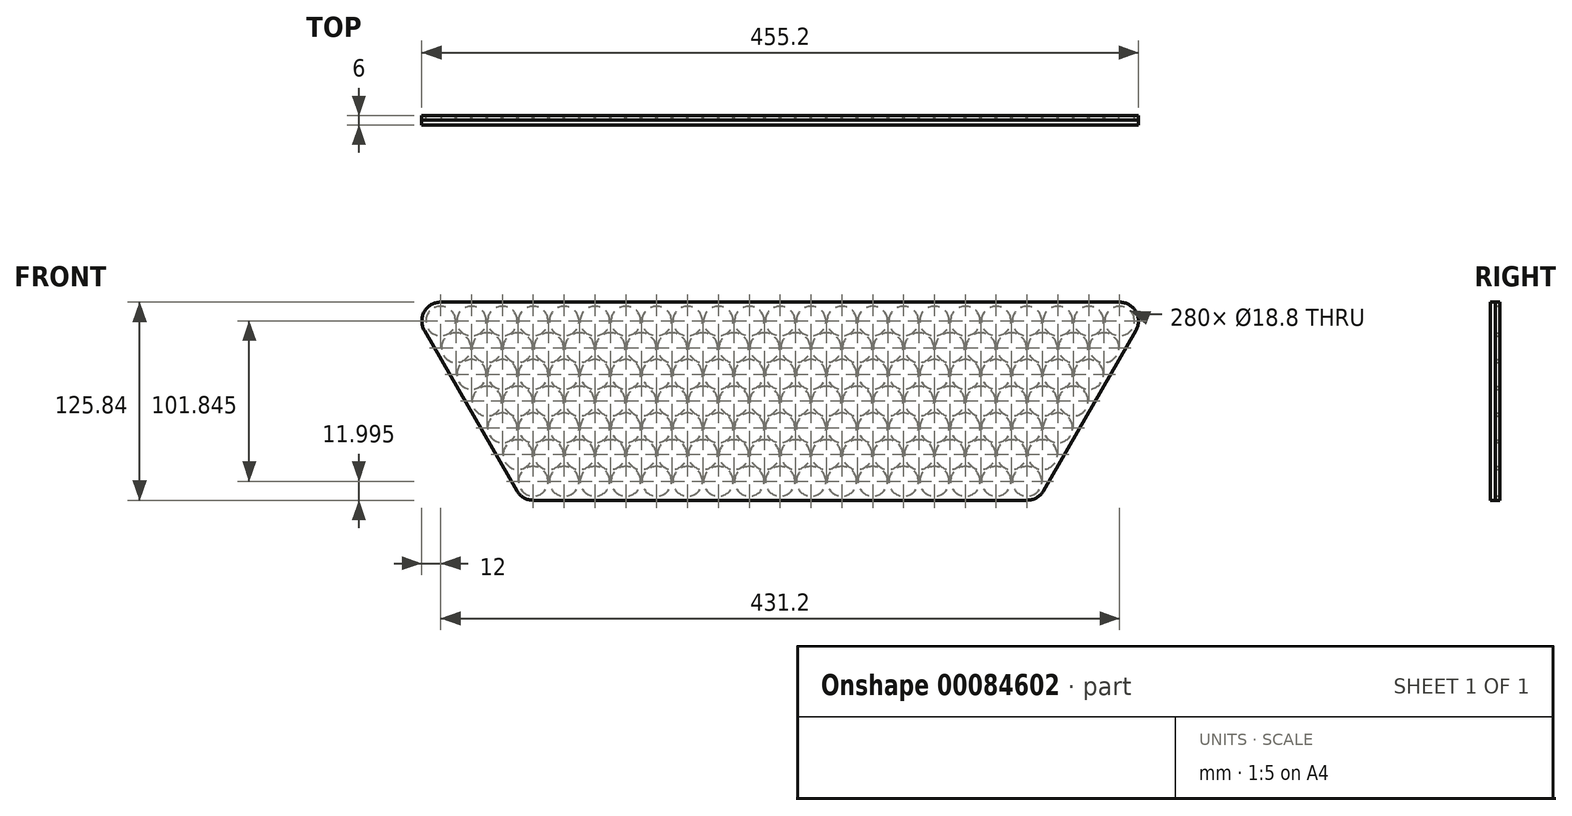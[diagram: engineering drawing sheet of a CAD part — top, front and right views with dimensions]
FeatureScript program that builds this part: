
annotation { "Feature Type Name" : "Feature", "Feature Type Description" : "" }
export const myFeature = defineFeature(function(context is Context, id is Id, definition is map)
    precondition{}
    {
        {
            var Q0;
            Q0=qCreatedBy(makeId("Front.planeOp"),FACE);
            var sketch = newSketch(context, id + "F0", { "sketchPlane" : qUnion([Q0]) });
            skLineSegment(sketch, "E0", {"start": v(0, 0) * mm, "end": v(79.44, 0) * mm, "construction": true});
            skLineSegment(sketch, "E1", {"start": v(0, 0) * mm, "end": v(43.4, -75.16) * mm, "construction": true});
            skCircle(sketch, "E2", {"center": v(0, 0) * mm, "radius": 9.4 * mm});
            skCircle(sketch, "E3.1.0.0", {"center": v(19.6, 0) * mm, "radius": 9.4 * mm});
            skCircle(sketch, "E3.2.0.0", {"center": v(39.2, 0) * mm, "radius": 9.4 * mm});
            skCircle(sketch, "E3.3.0.0", {"center": v(58.8, 0) * mm, "radius": 9.4 * mm});
            skCircle(sketch, "E3.4.0.0", {"center": v(78.4, 0) * mm, "radius": 9.4 * mm});
            skCircle(sketch, "E3.5.0.0", {"center": v(98, 0) * mm, "radius": 9.4 * mm});
            skCircle(sketch, "E3.6.0.0", {"center": v(117.6, 0) * mm, "radius": 9.4 * mm});
            skCircle(sketch, "E3.7.0.0", {"center": v(137.2, 0) * mm, "radius": 9.4 * mm});
            skCircle(sketch, "E3.8.0.0", {"center": v(156.8, 0) * mm, "radius": 9.4 * mm});
            skCircle(sketch, "E3.9.0.0", {"center": v(176.4, 0) * mm, "radius": 9.4 * mm});
            skCircle(sketch, "E3.10.0.0", {"center": v(196, 0) * mm, "radius": 9.4 * mm});
            skCircle(sketch, "E3.11.0.0", {"center": v(215.6, 0) * mm, "radius": 9.4 * mm});
            skCircle(sketch, "E3.12.0.0", {"center": v(235.2, 0) * mm, "radius": 9.4 * mm});
            skCircle(sketch, "E3.13.0.0", {"center": v(254.8, 0) * mm, "radius": 9.4 * mm});
            skCircle(sketch, "E3.14.0.0", {"center": v(274.4, 0) * mm, "radius": 9.4 * mm});
            skCircle(sketch, "E3.15.0.0", {"center": v(294, 0) * mm, "radius": 9.4 * mm});
            skCircle(sketch, "E3.16.0.0", {"center": v(313.6, 0) * mm, "radius": 9.4 * mm});
            skCircle(sketch, "E3.17.0.0", {"center": v(333.2, 0) * mm, "radius": 9.4 * mm});
            skCircle(sketch, "E3.18.0.0", {"center": v(352.8, 0) * mm, "radius": 9.4 * mm});
            skCircle(sketch, "E3.19.0.0", {"center": v(372.4, 0) * mm, "radius": 9.4 * mm});
            skLineSegment(sketch, "E3.direction1", {"start": v(0, 0) * mm, "end": v(19.6, 0) * mm, "construction": true});
            skCircle(sketch, "E4.1.0.0", {"center": v(9.8, -16.97) * mm, "radius": 9.4 * mm});
            skCircle(sketch, "E4.2.0.0", {"center": v(19.6, -33.95) * mm, "radius": 9.4 * mm});
            skCircle(sketch, "E4.3.0.0", {"center": v(29.4, -50.92) * mm, "radius": 9.4 * mm});
            skCircle(sketch, "E4.4.0.0", {"center": v(39.2, -67.9) * mm, "radius": 9.4 * mm});
            skCircle(sketch, "E4.5.0.0", {"center": v(49, -84.87) * mm, "radius": 9.4 * mm});
            skCircle(sketch, "E4.6.0.0", {"center": v(58.8, -101.84) * mm, "radius": 9.4 * mm});
            skLineSegment(sketch, "E4.direction1", {"start": v(0, 0) * mm, "end": v(9.8, -16.97) * mm, "construction": true});
            skCircle(sketch, "E5.1.0.0", {"center": v(29.4, -16.97) * mm, "radius": 9.4 * mm});
            skCircle(sketch, "E5.1.0.1", {"center": v(39.2, -33.95) * mm, "radius": 9.4 * mm});
            skCircle(sketch, "E5.1.0.2", {"center": v(49, -50.92) * mm, "radius": 9.4 * mm});
            skCircle(sketch, "E5.1.0.3", {"center": v(58.8, -67.9) * mm, "radius": 9.4 * mm});
            skCircle(sketch, "E5.1.0.4", {"center": v(68.6, -84.87) * mm, "radius": 9.4 * mm});
            skCircle(sketch, "E5.1.0.5", {"center": v(78.4, -101.84) * mm, "radius": 9.4 * mm});
            skCircle(sketch, "E5.2.0.0", {"center": v(49, -16.97) * mm, "radius": 9.4 * mm});
            skCircle(sketch, "E5.2.0.1", {"center": v(58.8, -33.95) * mm, "radius": 9.4 * mm});
            skCircle(sketch, "E5.2.0.2", {"center": v(68.6, -50.92) * mm, "radius": 9.4 * mm});
            skCircle(sketch, "E5.2.0.3", {"center": v(78.4, -67.9) * mm, "radius": 9.4 * mm});
            skCircle(sketch, "E5.2.0.4", {"center": v(88.2, -84.87) * mm, "radius": 9.4 * mm});
            skCircle(sketch, "E5.2.0.5", {"center": v(98, -101.84) * mm, "radius": 9.4 * mm});
            skCircle(sketch, "E5.3.0.0", {"center": v(68.6, -16.97) * mm, "radius": 9.4 * mm});
            skCircle(sketch, "E5.3.0.1", {"center": v(78.4, -33.95) * mm, "radius": 9.4 * mm});
            skCircle(sketch, "E5.3.0.2", {"center": v(88.2, -50.92) * mm, "radius": 9.4 * mm});
            skCircle(sketch, "E5.3.0.3", {"center": v(98, -67.9) * mm, "radius": 9.4 * mm});
            skCircle(sketch, "E5.3.0.4", {"center": v(107.8, -84.87) * mm, "radius": 9.4 * mm});
            skCircle(sketch, "E5.3.0.5", {"center": v(117.6, -101.84) * mm, "radius": 9.4 * mm});
            skCircle(sketch, "E5.4.0.0", {"center": v(88.2, -16.97) * mm, "radius": 9.4 * mm});
            skCircle(sketch, "E5.4.0.1", {"center": v(98, -33.95) * mm, "radius": 9.4 * mm});
            skCircle(sketch, "E5.4.0.2", {"center": v(107.8, -50.92) * mm, "radius": 9.4 * mm});
            skCircle(sketch, "E5.4.0.3", {"center": v(117.6, -67.9) * mm, "radius": 9.4 * mm});
            skCircle(sketch, "E5.4.0.4", {"center": v(127.4, -84.87) * mm, "radius": 9.4 * mm});
            skCircle(sketch, "E5.4.0.5", {"center": v(137.2, -101.84) * mm, "radius": 9.4 * mm});
            skCircle(sketch, "E5.5.0.0", {"center": v(107.8, -16.97) * mm, "radius": 9.4 * mm});
            skCircle(sketch, "E5.5.0.1", {"center": v(117.6, -33.95) * mm, "radius": 9.4 * mm});
            skCircle(sketch, "E5.5.0.2", {"center": v(127.4, -50.92) * mm, "radius": 9.4 * mm});
            skCircle(sketch, "E5.5.0.3", {"center": v(137.2, -67.9) * mm, "radius": 9.4 * mm});
            skCircle(sketch, "E5.5.0.4", {"center": v(147, -84.87) * mm, "radius": 9.4 * mm});
            skCircle(sketch, "E5.5.0.5", {"center": v(156.8, -101.84) * mm, "radius": 9.4 * mm});
            skCircle(sketch, "E5.6.0.0", {"center": v(127.4, -16.97) * mm, "radius": 9.4 * mm});
            skCircle(sketch, "E5.6.0.1", {"center": v(137.2, -33.95) * mm, "radius": 9.4 * mm});
            skCircle(sketch, "E5.6.0.2", {"center": v(147, -50.92) * mm, "radius": 9.4 * mm});
            skCircle(sketch, "E5.6.0.3", {"center": v(156.8, -67.9) * mm, "radius": 9.4 * mm});
            skCircle(sketch, "E5.6.0.4", {"center": v(166.6, -84.87) * mm, "radius": 9.4 * mm});
            skCircle(sketch, "E5.6.0.5", {"center": v(176.4, -101.84) * mm, "radius": 9.4 * mm});
            skCircle(sketch, "E5.7.0.0", {"center": v(147, -16.97) * mm, "radius": 9.4 * mm});
            skCircle(sketch, "E5.7.0.1", {"center": v(156.8, -33.95) * mm, "radius": 9.4 * mm});
            skCircle(sketch, "E5.7.0.2", {"center": v(166.6, -50.92) * mm, "radius": 9.4 * mm});
            skCircle(sketch, "E5.7.0.3", {"center": v(176.4, -67.9) * mm, "radius": 9.4 * mm});
            skCircle(sketch, "E5.7.0.4", {"center": v(186.2, -84.87) * mm, "radius": 9.4 * mm});
            skCircle(sketch, "E5.7.0.5", {"center": v(196, -101.84) * mm, "radius": 9.4 * mm});
            skCircle(sketch, "E5.8.0.0", {"center": v(166.6, -16.97) * mm, "radius": 9.4 * mm});
            skCircle(sketch, "E5.8.0.1", {"center": v(176.4, -33.95) * mm, "radius": 9.4 * mm});
            skCircle(sketch, "E5.8.0.2", {"center": v(186.2, -50.92) * mm, "radius": 9.4 * mm});
            skCircle(sketch, "E5.8.0.3", {"center": v(196, -67.9) * mm, "radius": 9.4 * mm});
            skCircle(sketch, "E5.8.0.4", {"center": v(205.8, -84.87) * mm, "radius": 9.4 * mm});
            skCircle(sketch, "E5.8.0.5", {"center": v(215.6, -101.84) * mm, "radius": 9.4 * mm});
            skCircle(sketch, "E5.9.0.0", {"center": v(186.2, -16.97) * mm, "radius": 9.4 * mm});
            skCircle(sketch, "E5.9.0.1", {"center": v(196, -33.95) * mm, "radius": 9.4 * mm});
            skCircle(sketch, "E5.9.0.2", {"center": v(205.8, -50.92) * mm, "radius": 9.4 * mm});
            skCircle(sketch, "E5.9.0.3", {"center": v(215.6, -67.9) * mm, "radius": 9.4 * mm});
            skCircle(sketch, "E5.9.0.4", {"center": v(225.4, -84.87) * mm, "radius": 9.4 * mm});
            skCircle(sketch, "E5.9.0.5", {"center": v(235.2, -101.84) * mm, "radius": 9.4 * mm});
            skCircle(sketch, "E5.10.0.0", {"center": v(205.8, -16.97) * mm, "radius": 9.4 * mm});
            skCircle(sketch, "E5.10.0.1", {"center": v(215.6, -33.95) * mm, "radius": 9.4 * mm});
            skCircle(sketch, "E5.10.0.2", {"center": v(225.4, -50.92) * mm, "radius": 9.4 * mm});
            skCircle(sketch, "E5.10.0.3", {"center": v(235.2, -67.9) * mm, "radius": 9.4 * mm});
            skCircle(sketch, "E5.10.0.4", {"center": v(245, -84.87) * mm, "radius": 9.4 * mm});
            skCircle(sketch, "E5.10.0.5", {"center": v(254.8, -101.84) * mm, "radius": 9.4 * mm});
            skCircle(sketch, "E5.11.0.0", {"center": v(225.4, -16.97) * mm, "radius": 9.4 * mm});
            skCircle(sketch, "E5.11.0.1", {"center": v(235.2, -33.95) * mm, "radius": 9.4 * mm});
            skCircle(sketch, "E5.11.0.2", {"center": v(245, -50.92) * mm, "radius": 9.4 * mm});
            skCircle(sketch, "E5.11.0.3", {"center": v(254.8, -67.9) * mm, "radius": 9.4 * mm});
            skCircle(sketch, "E5.11.0.4", {"center": v(264.6, -84.87) * mm, "radius": 9.4 * mm});
            skCircle(sketch, "E5.11.0.5", {"center": v(274.4, -101.84) * mm, "radius": 9.4 * mm});
            skCircle(sketch, "E5.12.0.0", {"center": v(245, -16.97) * mm, "radius": 9.4 * mm});
            skCircle(sketch, "E5.12.0.1", {"center": v(254.8, -33.95) * mm, "radius": 9.4 * mm});
            skCircle(sketch, "E5.12.0.2", {"center": v(264.6, -50.92) * mm, "radius": 9.4 * mm});
            skCircle(sketch, "E5.12.0.3", {"center": v(274.4, -67.9) * mm, "radius": 9.4 * mm});
            skCircle(sketch, "E5.12.0.4", {"center": v(284.2, -84.87) * mm, "radius": 9.4 * mm});
            skCircle(sketch, "E5.12.0.5", {"center": v(294, -101.84) * mm, "radius": 9.4 * mm});
            skCircle(sketch, "E5.13.0.0", {"center": v(264.6, -16.97) * mm, "radius": 9.4 * mm});
            skCircle(sketch, "E5.13.0.1", {"center": v(274.4, -33.95) * mm, "radius": 9.4 * mm});
            skCircle(sketch, "E5.13.0.2", {"center": v(284.2, -50.92) * mm, "radius": 9.4 * mm});
            skCircle(sketch, "E5.13.0.3", {"center": v(294, -67.9) * mm, "radius": 9.4 * mm});
            skCircle(sketch, "E5.13.0.4", {"center": v(303.8, -84.87) * mm, "radius": 9.4 * mm});
            skCircle(sketch, "E5.13.0.5", {"center": v(313.6, -101.84) * mm, "radius": 9.4 * mm});
            skCircle(sketch, "E5.14.0.0", {"center": v(284.2, -16.97) * mm, "radius": 9.4 * mm});
            skCircle(sketch, "E5.14.0.1", {"center": v(294, -33.95) * mm, "radius": 9.4 * mm});
            skCircle(sketch, "E5.14.0.2", {"center": v(303.8, -50.92) * mm, "radius": 9.4 * mm});
            skCircle(sketch, "E5.14.0.3", {"center": v(313.6, -67.9) * mm, "radius": 9.4 * mm});
            skCircle(sketch, "E5.14.0.4", {"center": v(323.4, -84.87) * mm, "radius": 9.4 * mm});
            skCircle(sketch, "E5.14.0.5", {"center": v(333.2, -101.84) * mm, "radius": 9.4 * mm});
            skCircle(sketch, "E5.15.0.0", {"center": v(303.8, -16.97) * mm, "radius": 9.4 * mm});
            skCircle(sketch, "E5.15.0.1", {"center": v(313.6, -33.95) * mm, "radius": 9.4 * mm});
            skCircle(sketch, "E5.15.0.2", {"center": v(323.4, -50.92) * mm, "radius": 9.4 * mm});
            skCircle(sketch, "E5.15.0.3", {"center": v(333.2, -67.9) * mm, "radius": 9.4 * mm});
            skCircle(sketch, "E5.15.0.4", {"center": v(343, -84.87) * mm, "radius": 9.4 * mm});
            skCircle(sketch, "E5.15.0.5", {"center": v(352.8, -101.84) * mm, "radius": 9.4 * mm});
            skCircle(sketch, "E5.16.0.0", {"center": v(323.4, -16.97) * mm, "radius": 9.4 * mm});
            skCircle(sketch, "E5.16.0.1", {"center": v(333.2, -33.95) * mm, "radius": 9.4 * mm});
            skCircle(sketch, "E5.16.0.2", {"center": v(343, -50.92) * mm, "radius": 9.4 * mm});
            skCircle(sketch, "E5.16.0.3", {"center": v(352.8, -67.9) * mm, "radius": 9.4 * mm});
            skCircle(sketch, "E5.16.0.4", {"center": v(362.6, -84.87) * mm, "radius": 9.4 * mm});
            skCircle(sketch, "E5.16.0.5", {"center": v(372.4, -101.84) * mm, "radius": 9.4 * mm});
            skCircle(sketch, "E5.17.0.0", {"center": v(343, -16.97) * mm, "radius": 9.4 * mm});
            skCircle(sketch, "E5.17.0.1", {"center": v(352.8, -33.95) * mm, "radius": 9.4 * mm});
            skCircle(sketch, "E5.17.0.2", {"center": v(362.6, -50.92) * mm, "radius": 9.4 * mm});
            skCircle(sketch, "E5.17.0.3", {"center": v(372.4, -67.9) * mm, "radius": 9.4 * mm});
            skCircle(sketch, "E5.17.0.4", {"center": v(382.2, -84.87) * mm, "radius": 9.4 * mm});
            skCircle(sketch, "E5.18.0.0", {"center": v(362.6, -16.97) * mm, "radius": 9.4 * mm});
            skCircle(sketch, "E5.18.0.1", {"center": v(372.4, -33.95) * mm, "radius": 9.4 * mm});
            skCircle(sketch, "E5.18.0.2", {"center": v(382.2, -50.92) * mm, "radius": 9.4 * mm});
            skCircle(sketch, "E5.18.0.3", {"center": v(392, -67.9) * mm, "radius": 9.4 * mm});
            skCircle(sketch, "E5.19.0.0", {"center": v(382.2, -16.97) * mm, "radius": 9.4 * mm});
            skCircle(sketch, "E5.19.0.1", {"center": v(392, -33.95) * mm, "radius": 9.4 * mm});
            skCircle(sketch, "E5.19.0.2", {"center": v(401.8, -50.92) * mm, "radius": 9.4 * mm});
            skLineSegment(sketch, "E5.direction1", {"start": v(9.8, -16.97) * mm, "end": v(29.4, -16.97) * mm, "construction": true});
            skLineSegment(sketch, "E6", {"start": v(0, 0) * mm, "end": v(372.4, 0) * mm, "construction": true});
            skLineSegment(sketch, "E7", {"start": v(372.4, 0) * mm, "end": v(441, -118.82) * mm, "construction": true});
            skLineSegment(sketch, "E8", {"start": v(58.8, -101.84) * mm, "end": v(0, 0) * mm, "construction": true});
            skLineSegment(sketch, "E9", {"start": v(58.8, -101.84) * mm, "end": v(431.2, -101.84) * mm, "construction": true});
            skCircle(sketch, "E10.1.0.0", {"center": v(392, 0) * mm, "radius": 9.4 * mm});
            skCircle(sketch, "E10.2.0.0", {"center": v(411.6, 0) * mm, "radius": 9.4 * mm});
            skCircle(sketch, "E10.3.0.0", {"center": v(431.2, 0) * mm, "radius": 9.4 * mm});
            skLineSegment(sketch, "E10.direction1", {"start": v(372.4, 0) * mm, "end": v(392, 0) * mm, "construction": true});
            skCircle(sketch, "E11.1.0.0", {"center": v(401.8, -16.97) * mm, "radius": 9.4 * mm});
            skCircle(sketch, "E11.2.0.0", {"center": v(421.4, -16.97) * mm, "radius": 9.4 * mm});
            skLineSegment(sketch, "E11.direction1", {"start": v(382.2, -16.97) * mm, "end": v(401.8, -16.97) * mm, "construction": true});
            skCircle(sketch, "E12.1.0.0", {"center": v(411.6, -33.95) * mm, "radius": 9.4 * mm});
            skLineSegment(sketch, "E12.direction1", {"start": v(392, -33.95) * mm, "end": v(411.6, -33.95) * mm, "construction": true});
            skArc(sketch, "E13", {"start": v(441.6, -6) * mm, "mid": v(441.6, 6) * mm, "end": v(431.2, 12) * mm});
            skArc(sketch, "E14", {"start": v(372.4, -113.84) * mm, "mid": v(378.4, -112.24) * mm, "end": v(382.8, -107.84) * mm});
            skArc(sketch, "E15", {"start": v(0, 12) * mm, "mid": v(-10.4, 6) * mm, "end": v(-10.4, -6) * mm});
            skArc(sketch, "E16", {"start": v(48.4, -107.84) * mm, "mid": v(52.8, -112.24) * mm, "end": v(58.8, -113.84) * mm});
            skLineSegment(sketch, "E17", {"start": v(441.6, -6) * mm, "end": v(382.8, -107.84) * mm});
            skLineSegment(sketch, "E18", {"start": v(0, 12) * mm, "end": v(431.2, 12) * mm});
            skLineSegment(sketch, "E19", {"start": v(-10.4, -6) * mm, "end": v(48.4, -107.84) * mm});
            skLineSegment(sketch, "E20", {"start": v(58.8, -113.84) * mm, "end": v(372.4, -113.84) * mm});
            skSolve(sketch);
        }
        {
            var Q0;
            Q0=makeQuery(id+"F0.imprint","IMPRINT",FACE,{"disambiguationData":[TD([[makeQuery(id+"F0.imprint","IMPRINT",EDGE,{"derivedFrom":sQuery(id+"F0.wireOp",EDGE,"E2")}),-1.0]])]});
            extrude(context, id + "F1", {"entities" : qUnion([Q0]), "depth" : 3 * mm});
        }
        {
            var Q0;
            Q0=makeQuery(id+"F1.opExtrude","CAP_FACE",FACE,{"disambiguationData":[OSD([sQuery(id+"F0.wireOp",EDGE,"E2"),sQuery(id+"F0.wireOp",EDGE,"E3.1.0.0"),sQuery(id+"F0.wireOp",EDGE,"E3.2.0.0"),sQuery(id+"F0.wireOp",EDGE,"E3.3.0.0"),sQuery(id+"F0.wireOp",EDGE,"E3.4.0.0"),sQuery(id+"F0.wireOp",EDGE,"E3.5.0.0"),sQuery(id+"F0.wireOp",EDGE,"E3.6.0.0"),sQuery(id+"F0.wireOp",EDGE,"E3.7.0.0"),sQuery(id+"F0.wireOp",EDGE,"E3.8.0.0"),sQuery(id+"F0.wireOp",EDGE,"E3.9.0.0"),sQuery(id+"F0.wireOp",EDGE,"E3.10.0.0"),sQuery(id+"F0.wireOp",EDGE,"E3.11.0.0"),sQuery(id+"F0.wireOp",EDGE,"E3.12.0.0"),sQuery(id+"F0.wireOp",EDGE,"E3.13.0.0"),sQuery(id+"F0.wireOp",EDGE,"E3.14.0.0"),sQuery(id+"F0.wireOp",EDGE,"E3.15.0.0"),sQuery(id+"F0.wireOp",EDGE,"E3.16.0.0"),sQuery(id+"F0.wireOp",EDGE,"E3.17.0.0"),sQuery(id+"F0.wireOp",EDGE,"E3.18.0.0"),sQuery(id+"F0.wireOp",EDGE,"E3.19.0.0"),sQuery(id+"F0.wireOp",EDGE,"E4.1.0.0"),sQuery(id+"F0.wireOp",EDGE,"E4.2.0.0"),sQuery(id+"F0.wireOp",EDGE,"E4.3.0.0"),sQuery(id+"F0.wireOp",EDGE,"E4.4.0.0"),sQuery(id+"F0.wireOp",EDGE,"E4.5.0.0"),sQuery(id+"F0.wireOp",EDGE,"E4.6.0.0"),sQuery(id+"F0.wireOp",EDGE,"E5.1.0.0"),sQuery(id+"F0.wireOp",EDGE,"E5.1.0.1"),sQuery(id+"F0.wireOp",EDGE,"E5.1.0.2"),sQuery(id+"F0.wireOp",EDGE,"E5.1.0.3"),sQuery(id+"F0.wireOp",EDGE,"E5.1.0.4"),sQuery(id+"F0.wireOp",EDGE,"E5.1.0.5"),sQuery(id+"F0.wireOp",EDGE,"E5.2.0.0"),sQuery(id+"F0.wireOp",EDGE,"E5.2.0.1"),sQuery(id+"F0.wireOp",EDGE,"E5.2.0.2"),sQuery(id+"F0.wireOp",EDGE,"E5.2.0.3"),sQuery(id+"F0.wireOp",EDGE,"E5.2.0.4"),sQuery(id+"F0.wireOp",EDGE,"E5.2.0.5"),sQuery(id+"F0.wireOp",EDGE,"E5.3.0.0"),sQuery(id+"F0.wireOp",EDGE,"E5.3.0.1"),sQuery(id+"F0.wireOp",EDGE,"E5.3.0.2"),sQuery(id+"F0.wireOp",EDGE,"E5.3.0.3"),sQuery(id+"F0.wireOp",EDGE,"E5.3.0.4"),sQuery(id+"F0.wireOp",EDGE,"E5.3.0.5"),sQuery(id+"F0.wireOp",EDGE,"E5.4.0.0"),sQuery(id+"F0.wireOp",EDGE,"E5.4.0.1"),sQuery(id+"F0.wireOp",EDGE,"E5.4.0.2"),sQuery(id+"F0.wireOp",EDGE,"E5.4.0.3"),sQuery(id+"F0.wireOp",EDGE,"E5.4.0.4"),sQuery(id+"F0.wireOp",EDGE,"E5.4.0.5"),sQuery(id+"F0.wireOp",EDGE,"E5.5.0.0"),sQuery(id+"F0.wireOp",EDGE,"E5.5.0.1"),sQuery(id+"F0.wireOp",EDGE,"E5.5.0.2"),sQuery(id+"F0.wireOp",EDGE,"E5.5.0.3"),sQuery(id+"F0.wireOp",EDGE,"E5.5.0.4"),sQuery(id+"F0.wireOp",EDGE,"E5.5.0.5"),sQuery(id+"F0.wireOp",EDGE,"E5.6.0.0"),sQuery(id+"F0.wireOp",EDGE,"E5.6.0.1"),sQuery(id+"F0.wireOp",EDGE,"E5.6.0.2"),sQuery(id+"F0.wireOp",EDGE,"E5.6.0.3"),sQuery(id+"F0.wireOp",EDGE,"E5.6.0.4"),sQuery(id+"F0.wireOp",EDGE,"E5.6.0.5"),sQuery(id+"F0.wireOp",EDGE,"E5.7.0.0"),sQuery(id+"F0.wireOp",EDGE,"E5.7.0.1"),sQuery(id+"F0.wireOp",EDGE,"E5.7.0.2"),sQuery(id+"F0.wireOp",EDGE,"E5.7.0.3"),sQuery(id+"F0.wireOp",EDGE,"E5.7.0.4"),sQuery(id+"F0.wireOp",EDGE,"E5.7.0.5"),sQuery(id+"F0.wireOp",EDGE,"E5.8.0.0"),sQuery(id+"F0.wireOp",EDGE,"E5.8.0.1"),sQuery(id+"F0.wireOp",EDGE,"E5.8.0.2"),sQuery(id+"F0.wireOp",EDGE,"E5.8.0.3"),sQuery(id+"F0.wireOp",EDGE,"E5.8.0.4"),sQuery(id+"F0.wireOp",EDGE,"E5.8.0.5"),sQuery(id+"F0.wireOp",EDGE,"E5.9.0.0"),sQuery(id+"F0.wireOp",EDGE,"E5.9.0.1"),sQuery(id+"F0.wireOp",EDGE,"E5.9.0.2"),sQuery(id+"F0.wireOp",EDGE,"E5.9.0.3"),sQuery(id+"F0.wireOp",EDGE,"E5.9.0.4"),sQuery(id+"F0.wireOp",EDGE,"E5.9.0.5"),sQuery(id+"F0.wireOp",EDGE,"E5.10.0.0"),sQuery(id+"F0.wireOp",EDGE,"E5.10.0.1"),sQuery(id+"F0.wireOp",EDGE,"E5.10.0.2"),sQuery(id+"F0.wireOp",EDGE,"E5.10.0.3"),sQuery(id+"F0.wireOp",EDGE,"E5.10.0.4"),sQuery(id+"F0.wireOp",EDGE,"E5.10.0.5"),sQuery(id+"F0.wireOp",EDGE,"E5.11.0.0"),sQuery(id+"F0.wireOp",EDGE,"E5.11.0.1"),sQuery(id+"F0.wireOp",EDGE,"E5.11.0.2"),sQuery(id+"F0.wireOp",EDGE,"E5.11.0.3"),sQuery(id+"F0.wireOp",EDGE,"E5.11.0.4"),sQuery(id+"F0.wireOp",EDGE,"E5.11.0.5"),sQuery(id+"F0.wireOp",EDGE,"E5.12.0.0"),sQuery(id+"F0.wireOp",EDGE,"E5.12.0.1"),sQuery(id+"F0.wireOp",EDGE,"E5.12.0.2"),sQuery(id+"F0.wireOp",EDGE,"E5.12.0.3"),sQuery(id+"F0.wireOp",EDGE,"E5.12.0.4"),sQuery(id+"F0.wireOp",EDGE,"E5.12.0.5"),sQuery(id+"F0.wireOp",EDGE,"E5.13.0.0"),sQuery(id+"F0.wireOp",EDGE,"E5.13.0.1"),sQuery(id+"F0.wireOp",EDGE,"E5.13.0.2"),sQuery(id+"F0.wireOp",EDGE,"E5.13.0.3"),sQuery(id+"F0.wireOp",EDGE,"E5.13.0.4"),sQuery(id+"F0.wireOp",EDGE,"E5.13.0.5"),sQuery(id+"F0.wireOp",EDGE,"E5.14.0.0"),sQuery(id+"F0.wireOp",EDGE,"E5.14.0.1"),sQuery(id+"F0.wireOp",EDGE,"E5.14.0.2"),sQuery(id+"F0.wireOp",EDGE,"E5.14.0.3"),sQuery(id+"F0.wireOp",EDGE,"E5.14.0.4"),sQuery(id+"F0.wireOp",EDGE,"E5.14.0.5"),sQuery(id+"F0.wireOp",EDGE,"E5.15.0.0"),sQuery(id+"F0.wireOp",EDGE,"E5.15.0.1"),sQuery(id+"F0.wireOp",EDGE,"E5.15.0.2"),sQuery(id+"F0.wireOp",EDGE,"E5.15.0.3"),sQuery(id+"F0.wireOp",EDGE,"E5.15.0.4"),sQuery(id+"F0.wireOp",EDGE,"E5.15.0.5"),sQuery(id+"F0.wireOp",EDGE,"E5.16.0.0"),sQuery(id+"F0.wireOp",EDGE,"E5.16.0.1"),sQuery(id+"F0.wireOp",EDGE,"E5.16.0.2"),sQuery(id+"F0.wireOp",EDGE,"E5.16.0.3"),sQuery(id+"F0.wireOp",EDGE,"E5.16.0.4"),sQuery(id+"F0.wireOp",EDGE,"E5.16.0.5"),sQuery(id+"F0.wireOp",EDGE,"E5.17.0.0"),sQuery(id+"F0.wireOp",EDGE,"E5.17.0.1"),sQuery(id+"F0.wireOp",EDGE,"E5.17.0.2"),sQuery(id+"F0.wireOp",EDGE,"E5.17.0.3"),sQuery(id+"F0.wireOp",EDGE,"E5.17.0.4"),sQuery(id+"F0.wireOp",EDGE,"E5.18.0.0"),sQuery(id+"F0.wireOp",EDGE,"E5.18.0.1"),sQuery(id+"F0.wireOp",EDGE,"E5.18.0.2"),sQuery(id+"F0.wireOp",EDGE,"E5.18.0.3"),sQuery(id+"F0.wireOp",EDGE,"E5.19.0.0"),sQuery(id+"F0.wireOp",EDGE,"E5.19.0.1"),sQuery(id+"F0.wireOp",EDGE,"E5.19.0.2"),sQuery(id+"F0.wireOp",EDGE,"E10.1.0.0"),sQuery(id+"F0.wireOp",EDGE,"E10.2.0.0"),sQuery(id+"F0.wireOp",EDGE,"E10.3.0.0"),sQuery(id+"F0.wireOp",EDGE,"E11.1.0.0"),sQuery(id+"F0.wireOp",EDGE,"E11.2.0.0"),sQuery(id+"F0.wireOp",EDGE,"E12.1.0.0"),sQuery(id+"F0.wireOp",EDGE,"E13"),sQuery(id+"F0.wireOp",EDGE,"E14"),sQuery(id+"F0.wireOp",EDGE,"E15"),sQuery(id+"F0.wireOp",EDGE,"E16"),sQuery(id+"F0.wireOp",EDGE,"E17"),sQuery(id+"F0.wireOp",EDGE,"E18"),sQuery(id+"F0.wireOp",EDGE,"E19"),sQuery(id+"F0.wireOp",EDGE,"E20")])],"isStart":false});
            var sketch = newSketch(context, id + "F2", { "sketchPlane" : qUnion([Q0]) });
            skArc(sketch, "E21.0", {"start": v(0, 12) * mm, "mid": v(-10.4, 6) * mm, "end": v(-10.4, -6) * mm});
            skLineSegment(sketch, "E21.1", {"start": v(0, 12) * mm, "end": v(431.2, 12) * mm});
            skLineSegment(sketch, "E21.2", {"start": v(-10.4, -6) * mm, "end": v(48.4, -107.84) * mm});
            skArc(sketch, "E21.3", {"start": v(48.4, -107.84) * mm, "mid": v(52.8, -112.24) * mm, "end": v(58.8, -113.84) * mm});
            skLineSegment(sketch, "E21.4", {"start": v(58.8, -113.84) * mm, "end": v(372.4, -113.84) * mm});
            skArc(sketch, "E21.5", {"start": v(441.6, -6) * mm, "mid": v(441.6, 6) * mm, "end": v(431.2, 12) * mm});
            skLineSegment(sketch, "E21.6", {"start": v(441.6, -6) * mm, "end": v(382.8, -107.84) * mm});
            skArc(sketch, "E21.7", {"start": v(372.4, -113.84) * mm, "mid": v(378.4, -112.24) * mm, "end": v(382.8, -107.84) * mm});
            skSolve(sketch);
        }
        {
            var Q0;
            Q0 = qSketchRegion(id + "F2", true);
            extrude(context, id + "F3", {"entities" : qUnion([Q0]), "depth" : 3 * mm});
        }
        {
            var Q0;
            Q0=makeQuery(id+"F1.opExtrude","SWEPT_BODY",BODY,{"disambiguationData":[OSD([sQuery(id+"F0.wireOp",EDGE,"E2"),sQuery(id+"F0.wireOp",EDGE,"E3.1.0.0"),sQuery(id+"F0.wireOp",EDGE,"E3.2.0.0"),sQuery(id+"F0.wireOp",EDGE,"E3.3.0.0"),sQuery(id+"F0.wireOp",EDGE,"E3.4.0.0"),sQuery(id+"F0.wireOp",EDGE,"E3.5.0.0"),sQuery(id+"F0.wireOp",EDGE,"E3.6.0.0"),sQuery(id+"F0.wireOp",EDGE,"E3.7.0.0"),sQuery(id+"F0.wireOp",EDGE,"E3.8.0.0"),sQuery(id+"F0.wireOp",EDGE,"E3.9.0.0"),sQuery(id+"F0.wireOp",EDGE,"E3.10.0.0"),sQuery(id+"F0.wireOp",EDGE,"E3.11.0.0"),sQuery(id+"F0.wireOp",EDGE,"E3.12.0.0"),sQuery(id+"F0.wireOp",EDGE,"E3.13.0.0"),sQuery(id+"F0.wireOp",EDGE,"E3.14.0.0"),sQuery(id+"F0.wireOp",EDGE,"E3.15.0.0"),sQuery(id+"F0.wireOp",EDGE,"E3.16.0.0"),sQuery(id+"F0.wireOp",EDGE,"E3.17.0.0"),sQuery(id+"F0.wireOp",EDGE,"E3.18.0.0"),sQuery(id+"F0.wireOp",EDGE,"E3.19.0.0"),sQuery(id+"F0.wireOp",EDGE,"E4.1.0.0"),sQuery(id+"F0.wireOp",EDGE,"E4.2.0.0"),sQuery(id+"F0.wireOp",EDGE,"E4.3.0.0"),sQuery(id+"F0.wireOp",EDGE,"E4.4.0.0"),sQuery(id+"F0.wireOp",EDGE,"E4.5.0.0"),sQuery(id+"F0.wireOp",EDGE,"E4.6.0.0"),sQuery(id+"F0.wireOp",EDGE,"E5.1.0.0"),sQuery(id+"F0.wireOp",EDGE,"E5.1.0.1"),sQuery(id+"F0.wireOp",EDGE,"E5.1.0.2"),sQuery(id+"F0.wireOp",EDGE,"E5.1.0.3"),sQuery(id+"F0.wireOp",EDGE,"E5.1.0.4"),sQuery(id+"F0.wireOp",EDGE,"E5.1.0.5"),sQuery(id+"F0.wireOp",EDGE,"E5.2.0.0"),sQuery(id+"F0.wireOp",EDGE,"E5.2.0.1"),sQuery(id+"F0.wireOp",EDGE,"E5.2.0.2"),sQuery(id+"F0.wireOp",EDGE,"E5.2.0.3"),sQuery(id+"F0.wireOp",EDGE,"E5.2.0.4"),sQuery(id+"F0.wireOp",EDGE,"E5.2.0.5"),sQuery(id+"F0.wireOp",EDGE,"E5.3.0.0"),sQuery(id+"F0.wireOp",EDGE,"E5.3.0.1"),sQuery(id+"F0.wireOp",EDGE,"E5.3.0.2"),sQuery(id+"F0.wireOp",EDGE,"E5.3.0.3"),sQuery(id+"F0.wireOp",EDGE,"E5.3.0.4"),sQuery(id+"F0.wireOp",EDGE,"E5.3.0.5"),sQuery(id+"F0.wireOp",EDGE,"E5.4.0.0"),sQuery(id+"F0.wireOp",EDGE,"E5.4.0.1"),sQuery(id+"F0.wireOp",EDGE,"E5.4.0.2"),sQuery(id+"F0.wireOp",EDGE,"E5.4.0.3"),sQuery(id+"F0.wireOp",EDGE,"E5.4.0.4"),sQuery(id+"F0.wireOp",EDGE,"E5.4.0.5"),sQuery(id+"F0.wireOp",EDGE,"E5.5.0.0"),sQuery(id+"F0.wireOp",EDGE,"E5.5.0.1"),sQuery(id+"F0.wireOp",EDGE,"E5.5.0.2"),sQuery(id+"F0.wireOp",EDGE,"E5.5.0.3"),sQuery(id+"F0.wireOp",EDGE,"E5.5.0.4"),sQuery(id+"F0.wireOp",EDGE,"E5.5.0.5"),sQuery(id+"F0.wireOp",EDGE,"E5.6.0.0"),sQuery(id+"F0.wireOp",EDGE,"E5.6.0.1"),sQuery(id+"F0.wireOp",EDGE,"E5.6.0.2"),sQuery(id+"F0.wireOp",EDGE,"E5.6.0.3"),sQuery(id+"F0.wireOp",EDGE,"E5.6.0.4"),sQuery(id+"F0.wireOp",EDGE,"E5.6.0.5"),sQuery(id+"F0.wireOp",EDGE,"E5.7.0.0"),sQuery(id+"F0.wireOp",EDGE,"E5.7.0.1"),sQuery(id+"F0.wireOp",EDGE,"E5.7.0.2"),sQuery(id+"F0.wireOp",EDGE,"E5.7.0.3"),sQuery(id+"F0.wireOp",EDGE,"E5.7.0.4"),sQuery(id+"F0.wireOp",EDGE,"E5.7.0.5"),sQuery(id+"F0.wireOp",EDGE,"E5.8.0.0"),sQuery(id+"F0.wireOp",EDGE,"E5.8.0.1"),sQuery(id+"F0.wireOp",EDGE,"E5.8.0.2"),sQuery(id+"F0.wireOp",EDGE,"E5.8.0.3"),sQuery(id+"F0.wireOp",EDGE,"E5.8.0.4"),sQuery(id+"F0.wireOp",EDGE,"E5.8.0.5"),sQuery(id+"F0.wireOp",EDGE,"E5.9.0.0"),sQuery(id+"F0.wireOp",EDGE,"E5.9.0.1"),sQuery(id+"F0.wireOp",EDGE,"E5.9.0.2"),sQuery(id+"F0.wireOp",EDGE,"E5.9.0.3"),sQuery(id+"F0.wireOp",EDGE,"E5.9.0.4"),sQuery(id+"F0.wireOp",EDGE,"E5.9.0.5"),sQuery(id+"F0.wireOp",EDGE,"E5.10.0.0"),sQuery(id+"F0.wireOp",EDGE,"E5.10.0.1"),sQuery(id+"F0.wireOp",EDGE,"E5.10.0.2"),sQuery(id+"F0.wireOp",EDGE,"E5.10.0.3"),sQuery(id+"F0.wireOp",EDGE,"E5.10.0.4"),sQuery(id+"F0.wireOp",EDGE,"E5.10.0.5"),sQuery(id+"F0.wireOp",EDGE,"E5.11.0.0"),sQuery(id+"F0.wireOp",EDGE,"E5.11.0.1"),sQuery(id+"F0.wireOp",EDGE,"E5.11.0.2"),sQuery(id+"F0.wireOp",EDGE,"E5.11.0.3"),sQuery(id+"F0.wireOp",EDGE,"E5.11.0.4"),sQuery(id+"F0.wireOp",EDGE,"E5.11.0.5"),sQuery(id+"F0.wireOp",EDGE,"E5.12.0.0"),sQuery(id+"F0.wireOp",EDGE,"E5.12.0.1"),sQuery(id+"F0.wireOp",EDGE,"E5.12.0.2"),sQuery(id+"F0.wireOp",EDGE,"E5.12.0.3"),sQuery(id+"F0.wireOp",EDGE,"E5.12.0.4"),sQuery(id+"F0.wireOp",EDGE,"E5.12.0.5"),sQuery(id+"F0.wireOp",EDGE,"E5.13.0.0"),sQuery(id+"F0.wireOp",EDGE,"E5.13.0.1"),sQuery(id+"F0.wireOp",EDGE,"E5.13.0.2"),sQuery(id+"F0.wireOp",EDGE,"E5.13.0.3"),sQuery(id+"F0.wireOp",EDGE,"E5.13.0.4"),sQuery(id+"F0.wireOp",EDGE,"E5.13.0.5"),sQuery(id+"F0.wireOp",EDGE,"E5.14.0.0"),sQuery(id+"F0.wireOp",EDGE,"E5.14.0.1"),sQuery(id+"F0.wireOp",EDGE,"E5.14.0.2"),sQuery(id+"F0.wireOp",EDGE,"E5.14.0.3"),sQuery(id+"F0.wireOp",EDGE,"E5.14.0.4"),sQuery(id+"F0.wireOp",EDGE,"E5.14.0.5"),sQuery(id+"F0.wireOp",EDGE,"E5.15.0.0"),sQuery(id+"F0.wireOp",EDGE,"E5.15.0.1"),sQuery(id+"F0.wireOp",EDGE,"E5.15.0.2"),sQuery(id+"F0.wireOp",EDGE,"E5.15.0.3"),sQuery(id+"F0.wireOp",EDGE,"E5.15.0.4"),sQuery(id+"F0.wireOp",EDGE,"E5.15.0.5"),sQuery(id+"F0.wireOp",EDGE,"E5.16.0.0"),sQuery(id+"F0.wireOp",EDGE,"E5.16.0.1"),sQuery(id+"F0.wireOp",EDGE,"E5.16.0.2"),sQuery(id+"F0.wireOp",EDGE,"E5.16.0.3"),sQuery(id+"F0.wireOp",EDGE,"E5.16.0.4"),sQuery(id+"F0.wireOp",EDGE,"E5.16.0.5"),sQuery(id+"F0.wireOp",EDGE,"E5.17.0.0"),sQuery(id+"F0.wireOp",EDGE,"E5.17.0.1"),sQuery(id+"F0.wireOp",EDGE,"E5.17.0.2"),sQuery(id+"F0.wireOp",EDGE,"E5.17.0.3"),sQuery(id+"F0.wireOp",EDGE,"E5.17.0.4"),sQuery(id+"F0.wireOp",EDGE,"E5.18.0.0"),sQuery(id+"F0.wireOp",EDGE,"E5.18.0.1"),sQuery(id+"F0.wireOp",EDGE,"E5.18.0.2"),sQuery(id+"F0.wireOp",EDGE,"E5.18.0.3"),sQuery(id+"F0.wireOp",EDGE,"E5.19.0.0"),sQuery(id+"F0.wireOp",EDGE,"E5.19.0.1"),sQuery(id+"F0.wireOp",EDGE,"E5.19.0.2"),sQuery(id+"F0.wireOp",EDGE,"E10.1.0.0"),sQuery(id+"F0.wireOp",EDGE,"E10.2.0.0"),sQuery(id+"F0.wireOp",EDGE,"E10.3.0.0"),sQuery(id+"F0.wireOp",EDGE,"E11.1.0.0"),sQuery(id+"F0.wireOp",EDGE,"E11.2.0.0"),sQuery(id+"F0.wireOp",EDGE,"E12.1.0.0"),sQuery(id+"F0.wireOp",EDGE,"E13"),sQuery(id+"F0.wireOp",EDGE,"E14"),sQuery(id+"F0.wireOp",EDGE,"E15"),sQuery(id+"F0.wireOp",EDGE,"E16"),sQuery(id+"F0.wireOp",EDGE,"E17"),sQuery(id+"F0.wireOp",EDGE,"E18"),sQuery(id+"F0.wireOp",EDGE,"E19"),sQuery(id+"F0.wireOp",EDGE,"E20")])]});
            transform(context, id + "F4", {"entities" : qUnion([Q0]), "transformType" : TransformType.TRANSLATION_3D, "dx" : 0 * mm, "dy" : 0 * mm, "dz" : 0 * mm, "makeCopy" : true});
        }
    });
